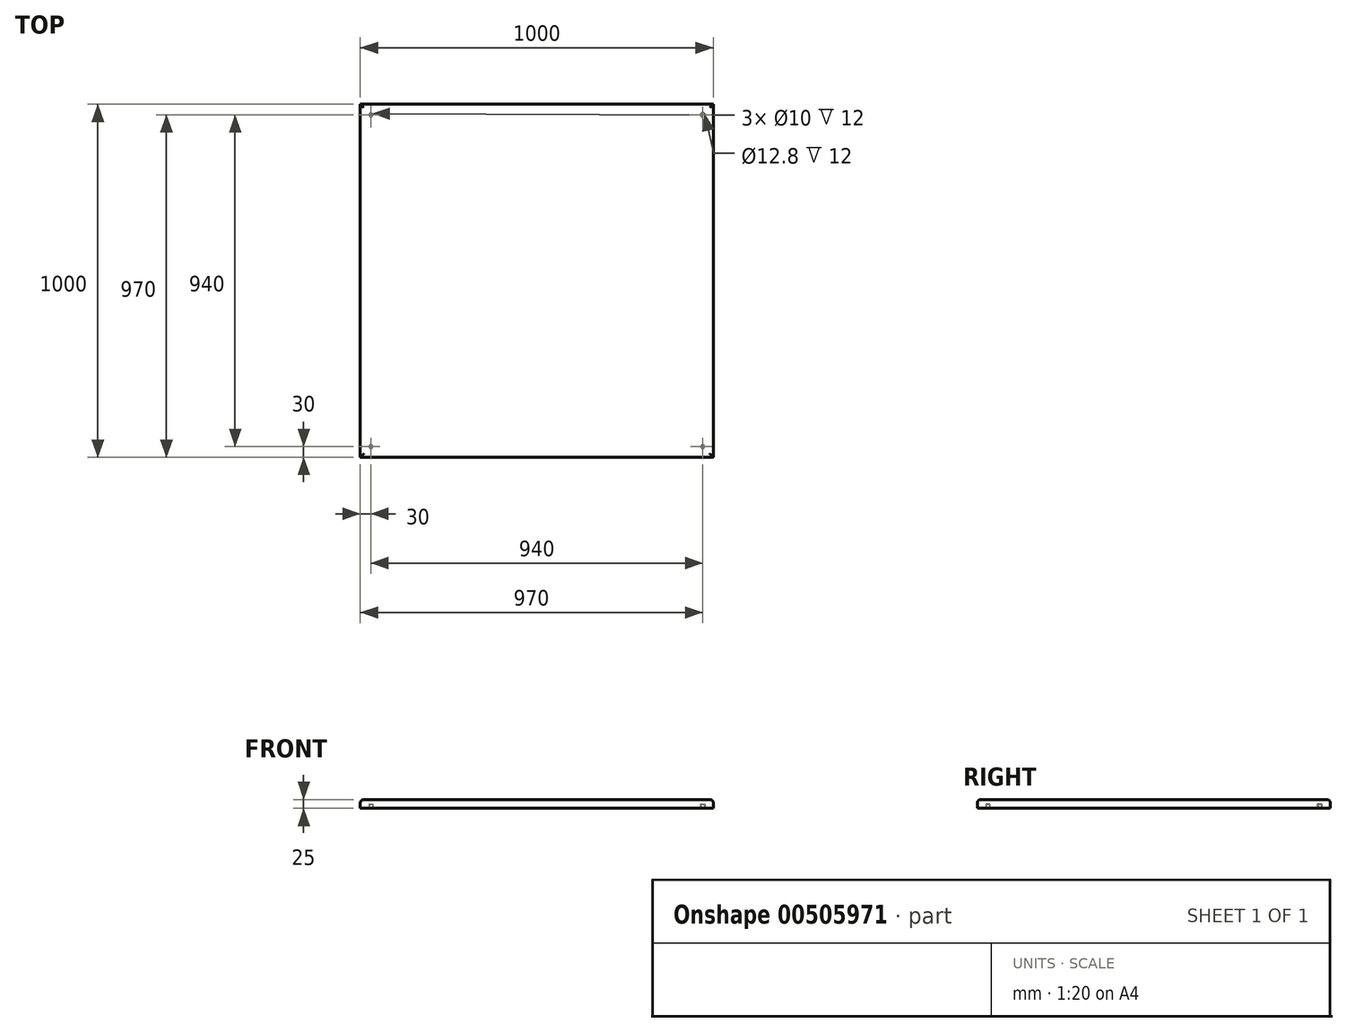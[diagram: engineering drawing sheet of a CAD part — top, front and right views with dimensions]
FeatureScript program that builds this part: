
annotation { "Feature Type Name" : "Feature", "Feature Type Description" : "" }
export const myFeature = defineFeature(function(context is Context, id is Id, definition is map)
    precondition{}
    {
        {
            var Q0;
            Q0=qCreatedBy(makeId("Front.planeOp"),FACE);
            var sketch = newSketch(context, id + "F0", { "sketchPlane" : qUnion([Q0])});
            skLineSegment(sketch, "E0.bottom", {"start": v(0, 0) * mm, "end": v(1000, 0) * mm});
            skLineSegment(sketch, "E0.top", {"start": v(0, 25) * mm, "end": v(1000, 25) * mm});
            skLineSegment(sketch, "E0.left", {"start": v(0, 0) * mm, "end": v(0, 25) * mm});
            skLineSegment(sketch, "E0.right", {"start": v(1000, 0) * mm, "end": v(1000, 25) * mm});
            skSolve(sketch);
        }
        {
            var Q0;
            Q0=makeQuery(id+"F0.imprint","IMPRINT",FACE,{"disambiguationData":[TD([[makeQuery(id+"F0.imprint","IMPRINT",EDGE,{"derivedFrom":sQuery(id+"F0.wireOp",EDGE,"E0.bottom")}),1.0]])]});
            extrude(context, id + "F1", {"entities" : qUnion([Q0]), "depth" : 1000 * mm, "offsetDistance" : 25 * mm});
        }
        {
            var Q0;
            Q0=makeQuery(id+"F1.opExtrude","CAP_EDGE",EDGE,{"disambiguationData":[OSD([sQuery(id+"F0.wireOp",EDGE,"E0.top")])],"isStart":false});
            var Q1;
            Q1=makeQuery(id+"F1.opExtrude","SWEPT_EDGE",EDGE,{"disambiguationData":[OSD([sQuery(id+"F0.wireOp",EDGE,"E0.top"),sQuery(id+"F0.wireOp",EDGE,"E0.right")])]});
            var Q2;
            Q2=makeQuery(id+"F1.opExtrude","CAP_EDGE",EDGE,{"disambiguationData":[OSD([sQuery(id+"F0.wireOp",EDGE,"E0.top")])],"isStart":true});
            var Q3;
            Q3=makeQuery(id+"F1.opExtrude","SWEPT_EDGE",EDGE,{"disambiguationData":[OSD([sQuery(id+"F0.wireOp",EDGE,"E0.top"),sQuery(id+"F0.wireOp",EDGE,"E0.left")])]});
            fillet(context, id + "F2", {"entities" : qUnion([Q0, Q1, Q2, Q3]), "radius" : 10 * mm, "tangentPropagation" : true, "allowEdgeOverflow" : false});
        }
        {
            var Q0;
            Q0=makeQuery(id+"F1.opExtrude","SWEPT_FACE",FACE,{"disambiguationData":[OSD([sQuery(id+"F0.wireOp",EDGE,"E0.bottom")])]});
            var sketch = newSketch(context, id + "F3", { "sketchPlane" : qUnion([Q0])});
            skCircle(sketch, "E1", {"center": v(30, 970) * mm, "radius": 5 * mm});
            skSolve(sketch);
        }
        {
            var Q0;
            Q0=makeQuery(id+"F3.imprint","IMPRINT",FACE,{"disambiguationData":[TD([[makeQuery(id+"F3.imprint","IMPRINT",EDGE,{"derivedFrom":sQuery(id+"F3.wireOp",EDGE,"E1")}),1.0]])]});
            extrude(context, id + "F4", {"entities" : qUnion([Q0]), "operationType" : NewBodyOperationType.REMOVE, "oppositeDirection" : true, "depth" : 12 * mm, "offsetDistance" : 25 * mm});
        }
        {
            var Q0;
            Q0=makeQuery(id+"F1.opExtrude","SWEPT_FACE",FACE,{"disambiguationData":[OSD([sQuery(id+"F0.wireOp",EDGE,"E0.bottom")])]});
            var sketch = newSketch(context, id + "F5", { "sketchPlane" : qUnion([Q0])});
            skCircle(sketch, "E2", {"center": v(970, 970) * mm, "radius": 5 * mm});
            skSolve(sketch);
        }
        {
            var Q0;
            Q0=makeQuery(id+"F5.imprint","IMPRINT",FACE,{"disambiguationData":[TD([[makeQuery(id+"F5.imprint","IMPRINT",EDGE,{"derivedFrom":sQuery(id+"F5.wireOp",EDGE,"E2")}),-1.0]])]});
            var sketch = newSketch(context, id + "F6", { "sketchPlane" : qUnion([Q0])});
            skCircle(sketch, "E3", {"center": v(970, 30) * mm, "radius": 6.4 * mm});
            skSolve(sketch);
        }
        {
            var Q0;
            Q0 = qSketchRegion(id + "F6", true);
            extrude(context, id + "F7", {"entities" : qUnion([Q0]), "operationType" : NewBodyOperationType.REMOVE, "oppositeDirection" : true, "depth" : 12 * mm, "offsetDistance" : 25 * mm});
        }
        {
            var Q0;
            Q0=makeQuery(id+"F5.imprint","IMPRINT",FACE,{"disambiguationData":[TD([[makeQuery(id+"F5.imprint","IMPRINT",EDGE,{"derivedFrom":sQuery(id+"F5.wireOp",EDGE,"E2")}),1.0]])]});
            extrude(context, id + "F8", {"entities" : qUnion([Q0]), "operationType" : NewBodyOperationType.REMOVE, "oppositeDirection" : true, "depth" : 12 * mm, "offsetDistance" : 25 * mm});
        }
        {
            var Q0;
            Q0=makeQuery(id+"F1.opExtrude","SWEPT_FACE",FACE,{"disambiguationData":[OSD([sQuery(id+"F0.wireOp",EDGE,"E0.bottom")])]});
            var sketch = newSketch(context, id + "F9", { "sketchPlane" : qUnion([Q0])});
            skCircle(sketch, "E4", {"center": v(30, 30) * mm, "radius": 5 * mm});
            skSolve(sketch);
        }
        {
            var Q0;
            Q0=makeQuery(id+"F9.imprint","IMPRINT",FACE,{"disambiguationData":[TD([[makeQuery(id+"F9.imprint","IMPRINT",EDGE,{"derivedFrom":sQuery(id+"F9.wireOp",EDGE,"E4")}),1.0]])]});
            extrude(context, id + "F10", {"entities" : qUnion([Q0]), "operationType" : NewBodyOperationType.REMOVE, "oppositeDirection" : true, "depth" : 12 * mm, "offsetDistance" : 25 * mm});
        }
    });
